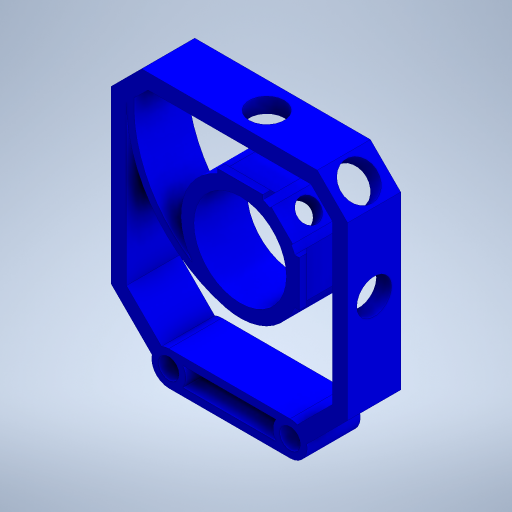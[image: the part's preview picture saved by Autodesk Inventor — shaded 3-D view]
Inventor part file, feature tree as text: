
AUTODESK INVENTOR PART (.ipt)
format: ipt  version: 2023.1 (Build 271208000, 208)  size: 462,336 bytes
history: native  units: mm
features: extrude x6, sketch x4, reference x3, projected_geometry x3, other x2, plane x1, mirror x1
ambient origin geometry x8: Origin, YZ Plane, XZ Plane, XY Plane, X Axis, Y Axis, Z Axis, Center Point
bodies: Solid1 (feature_tree)
feature tree (20):
  extrude  "Extrusion1"  Depth=1.25mm
  extrude  "Extrusion2"  TaperAngle=45.0deg  [1 undecoded]
  extrude  "Extrusion3"  Depth=0.675mm
  extrude  "Extrusion4"  Depth=10.0mm
  plane  "Work Plane1"
  mirror  "Mirror1"
  sketch  "Sketch5"  dims[d6=2.125mm d7=0.625mm d8=7.5mm d9=1.25mm d10=0.625mm d11=5.0mm d12=135.0deg d13=1.25mm d14=2.0mm d15=2.0mm d16=38.935534mm d17=38.935534mm d18=9.25mm d19=9.25mm d20=9.25mm d21=9.25mm d22=5.0mm d23=5.0mm d24=5.0mm d25=5.0mm d26=2.5mm d28=8.75mm d29=0.0mm d30=0.875mm d31=0.875mm d32=0.0mm d33=5.75mm d34=10.0mm d35=0.0mm d36=1.25mm d37=135.0deg d38=10.0mm d39=0.0mm d40=3.75mm d41=6.0mm d42=5.0mm d43=0.0mm d44=10.0mm d45=0.0mm d46=2.5mm d47=1.25mm d48=0.1425mm d49=0.1445mm]
  extrude  "Extrusion5"  Depth=10.0mm
  extrude  "Extrusion6"  Depth=10.0mm
  sketch  "Sketch1"  dims[d0=1.25mm d1=1.25mm]
  reference  "Reference1"
  reference  "Reference2"
  reference  "Reference3"
  sketch  "Sketch2"  dims[d2=2.5mm d3=45.0deg]
  sketch  "Sketch3"  dims[d4=15.25mm d5=0.675mm]
  projected_geometry  "Projected Loop1"
  projected_geometry  "Projected Loop2"
  projected_geometry  "Projected Loop4"
  other  "Cube 1x1 V5.iam"
  other  "Cube 1x1 Bottom V5:1"
note: 1 required parameter value undecoded (feature->parameter linkage not recoverable at this tier; creation-order binding heuristic only, values carry confidence <= 0.55)
